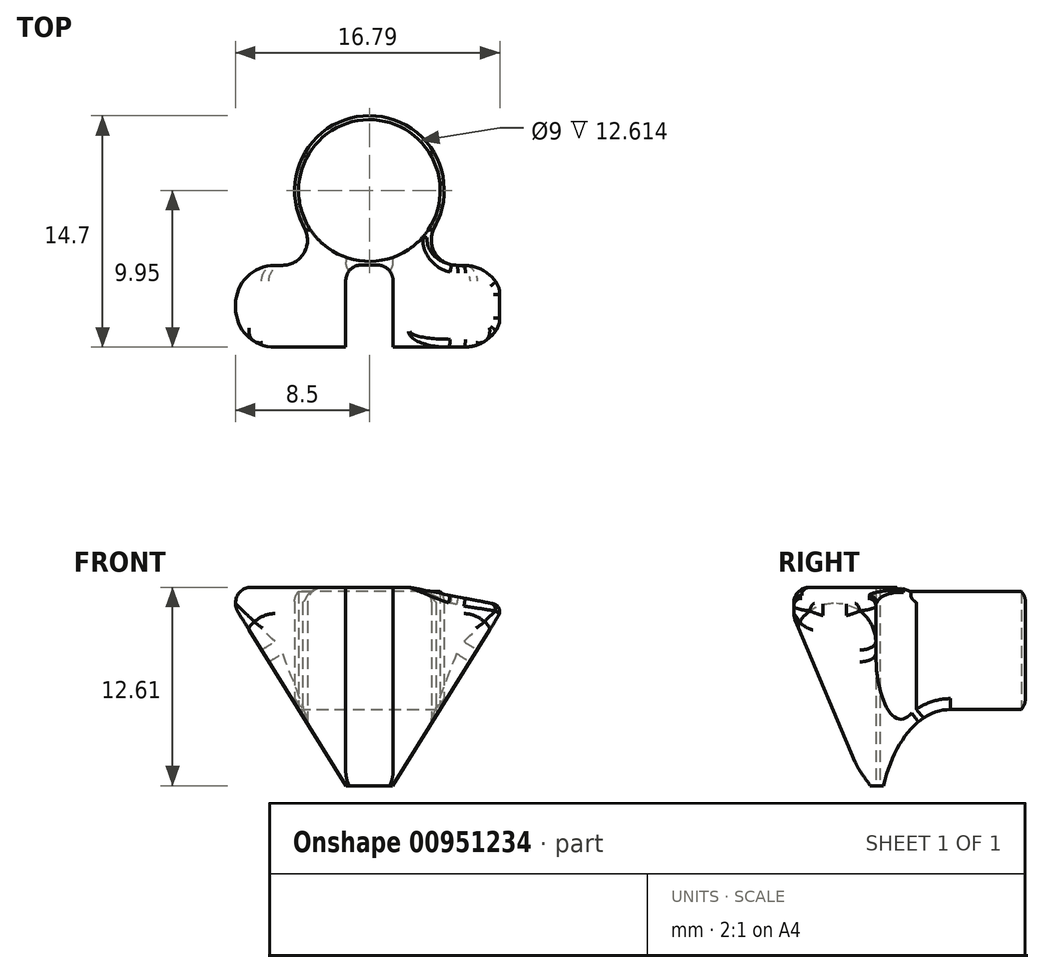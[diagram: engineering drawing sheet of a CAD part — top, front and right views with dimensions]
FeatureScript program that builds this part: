
annotation { "Feature Type Name" : "Feature", "Feature Type Description" : "" }
export const myFeature = defineFeature(function(context is Context, id is Id, definition is map)
    precondition{}
    {
        {
            var Q0;
            Q0=qCreatedBy(makeId("Top.planeOp"),FACE);
            var sketch = newSketch(context, id + "F0", { "sketchPlane" : qUnion([Q0])});
            skCircle(sketch, "E0", {"center": v(0, 0) * mm, "radius": 4.5 * mm});
            skArc(sketch, "E1", {"start": v(4.23, -2.16) * mm, "mid": v(0, 4.75) * mm, "end": v(-4.23, -2.16) * mm});
            skLineSegment(sketch, "E2", {"start": v(5.53, -4.75) * mm, "end": v(6, -4.75) * mm});
            skLineSegment(sketch, "E3", {"start": v(8.5, -7.25) * mm, "end": v(8.5, -7.45) * mm});
            skLineSegment(sketch, "E4", {"start": v(6, -9.95) * mm, "end": v(1.5, -9.95) * mm});
            skLineSegment(sketch, "E5", {"start": v(1.5, -9.95) * mm, "end": v(1.5, -5.73) * mm});
            skPoint(sketch, "E6.end.orphan", {"position": v(0, -5.25) * mm});
            skPoint(sketch, "E7.visualSharp", {"position": v(8.5, -4.75) * mm});
            skArc(sketch, "E7.filletArc", {"start": v(8.5, -7.25) * mm, "mid": v(7.77, -5.48) * mm, "end": v(6, -4.75) * mm});
            skPoint(sketch, "E8.visualSharp", {"position": v(8.5, -9.95) * mm});
            skArc(sketch, "E8.filletArc", {"start": v(6, -9.95) * mm, "mid": v(7.77, -9.22) * mm, "end": v(8.5, -7.45) * mm});
            skLineSegment(sketch, "E9", {"start": v(4.23, -2.16) * mm, "end": v(4.09, -2.46) * mm});
            skPoint(sketch, "E10.newPointA", {"position": v(3, -4.75) * mm});
            skPoint(sketch, "E10.newPointB", {"position": v(0, -4.75) * mm});
            skArc(sketch, "E10.filletArc", {"start": v(4.09, -2.46) * mm, "mid": v(4.18, -4) * mm, "end": v(5.53, -4.75) * mm});
            skLineSegment(sketch, "E11.MirrorCS", {"start": v(-1.5, -9.95) * mm, "end": v(-1.5, -5.73) * mm});
            skArc(sketch, "E12.MirrorCS", {"start": v(-4.09, -2.46) * mm, "mid": v(-4.18, -4) * mm, "end": v(-5.53, -4.75) * mm});
            skLineSegment(sketch, "E13.MirrorCS", {"start": v(-5.53, -4.75) * mm, "end": v(-6, -4.75) * mm});
            skLineSegment(sketch, "E14.MirrorCS", {"start": v(-4.23, -2.16) * mm, "end": v(-4.09, -2.46) * mm});
            skArc(sketch, "E15.MirrorCS", {"start": v(-8.5, -7.25) * mm, "mid": v(-7.77, -5.48) * mm, "end": v(-6, -4.75) * mm});
            skArc(sketch, "E16.MirrorCS", {"start": v(-6, -9.95) * mm, "mid": v(-7.77, -9.22) * mm, "end": v(-8.5, -7.45) * mm});
            skArc(sketch, "E17.trimOffspring", {"start": v(-0.41, -4.73) * mm, "mid": v(0, -4.75) * mm, "end": v(0.41, -4.73) * mm});
            skPoint(sketch, "E18.visualSharp", {"position": v(-1.5, -4.5) * mm});
            skArc(sketch, "E18.filletArc", {"start": v(-0.41, -4.73) * mm, "mid": v(-1.18, -5) * mm, "end": v(-1.5, -5.73) * mm});
            skPoint(sketch, "E19.visualSharp", {"position": v(1.5, -4.5) * mm});
            skArc(sketch, "E19.filletArc", {"start": v(1.5, -5.73) * mm, "mid": v(1.18, -5) * mm, "end": v(0.41, -4.73) * mm});
            skLineSegment(sketch, "E20.trimOffspring", {"start": v(-1.5, -9.95) * mm, "end": v(-6, -9.95) * mm});
            skLineSegment(sketch, "E21.MirrorCS", {"start": v(-8.5, -7.25) * mm, "end": v(-8.5, -7.45) * mm});
            skSolve(sketch);
        }
        {
            var Q0;
            Q0=makeQuery(id+"F0.imprint","IMPRINT",FACE,{"disambiguationData":[TD([[makeQuery(id+"F0.imprint","IMPRINT",EDGE,{"derivedFrom":sQuery(id+"F0.wireOp",EDGE,"E0")}),-1.0]])]});
            extrude(context, id + "F1", {"entities" : qUnion([Q0]), "depth" : 15 * mm, "offsetDistance" : 25 * mm});
        }
        {
            var Q0;
            Q0=qCreatedBy(makeId("Front.planeOp"),FACE);
            var sketch = newSketch(context, id + "F2", { "sketchPlane" : qUnion([Q0])});
            skLineSegment(sketch, "E22", {"start": v(0, 0) * mm, "end": v(-8.66, 13.94) * mm});
            skLineSegment(sketch, "E23", {"start": v(-8.66, 13.94) * mm, "end": v(-8.66, 0) * mm});
            skLineSegment(sketch, "E24", {"start": v(-8.66, 0) * mm, "end": v(0, 0) * mm});
            skLineSegment(sketch, "E25.MirrorCS", {"start": v(0, 0) * mm, "end": v(8.66, 13.94) * mm});
            skLineSegment(sketch, "E26.MirrorCS", {"start": v(8.66, 13.94) * mm, "end": v(8.66, 0) * mm});
            skLineSegment(sketch, "E27.MirrorCS", {"start": v(8.66, 0) * mm, "end": v(0, 0) * mm});
            skSolve(sketch);
        }
        {
            var Q0;
            Q0 = qSketchRegion(id + "F2", true);
            extrude(context, id + "F3", {"entities" : qUnion([Q0]), "operationType" : NewBodyOperationType.REMOVE, "depth" : 25 * mm, "offsetDistance" : 25 * mm});
        }
        {
            var Q0;
            Q0=qCreatedBy(makeId("Right.planeOp"),FACE);
            var sketch = newSketch(context, id + "F4", { "sketchPlane" : qUnion([Q0])});
            skLineSegment(sketch, "E28", {"start": v(-10.13, 13.54) * mm, "end": v(-5.41, 2.39) * mm});
            skLineSegment(sketch, "E29", {"start": v(-4.4, 0) * mm, "end": v(-11.01, 0) * mm});
            skLineSegment(sketch, "E30", {"start": v(-11.01, 0) * mm, "end": v(-11.01, 13.65) * mm});
            skLineSegment(sketch, "E31", {"start": v(-11.01, 13.65) * mm, "end": v(-10.13, 13.54) * mm});
            skLineSegment(sketch, "E32", {"start": v(0, 7.25) * mm, "end": v(5.54, 7.25) * mm});
            skLineSegment(sketch, "E33", {"start": v(5.54, 7.25) * mm, "end": v(5.54, -2.68) * mm});
            skLineSegment(sketch, "E34", {"start": v(5.54, -2.68) * mm, "end": v(0, -2.68) * mm});
            skLineSegment(sketch, "E35", {"start": v(0, -2.68) * mm, "end": v(0, 7.25) * mm});
            skLineSegment(sketch, "E36", {"start": v(-5.41, 2.39) * mm, "end": v(-3.47, 2.39) * mm});
            skLineSegment(sketch, "E37", {"start": v(-3.47, 2.39) * mm, "end": v(-3.47, 0) * mm});
            skLineSegment(sketch, "E38", {"start": v(-3.47, 0) * mm, "end": v(-4.7, 0) * mm});
            skSolve(sketch);
        }
        {
            var Q0;
            Q0 = qSketchRegion(id + "F4", true);
            extrude(context, id + "F5", {"entities" : qUnion([Q0]), "operationType" : NewBodyOperationType.REMOVE, "endBound" : BoundingType.SYMMETRIC, "oppositeDirection" : true, "depth" : 25 * mm, "offsetDistance" : 25 * mm});
        }
        {
            var Q0;
            Q0=makeQuery(id+"F5.boolean.opBoolean","INTERSECT",EDGE,{"disambiguationData":[OD(1.0)],"derivedFrom":[makeQuery(id+"F3.boolean.opBoolean","COPY",FACE,{"derivedFrom":makeQuery(id+"F3.opExtrude","SWEPT_FACE",FACE,{"disambiguationData":[OSD([sQuery(id+"F2.wireOp",EDGE,"E22")])]})}),makeQuery(id+"F5.opExtrude","SWEPT_FACE",FACE,{"disambiguationData":[OSD([sQuery(id+"F4.wireOp",EDGE,"E28")])]})]});
            var Q1;
            Q1=makeQuery(id+"F5.boolean.opBoolean","INTERSECT",EDGE,{"disambiguationData":[OD(1.0)],"derivedFrom":[makeQuery(id+"F3.boolean.opBoolean","COPY",FACE,{"derivedFrom":makeQuery(id+"F3.opExtrude","SWEPT_FACE",FACE,{"disambiguationData":[OSD([sQuery(id+"F2.wireOp",EDGE,"E25.MirrorCS")])]})}),makeQuery(id+"F5.opExtrude","SWEPT_FACE",FACE,{"disambiguationData":[OSD([sQuery(id+"F4.wireOp",EDGE,"E28")])]})]});
            var Q2;
            Q2=makeQuery(id+"F5.boolean.opBoolean","INTERSECT",EDGE,{"derivedFrom":[makeQuery(id+"F1.opExtrude","SWEPT_FACE",FACE,{"disambiguationData":[OSD([sQuery(id+"F0.wireOp",EDGE,"E4")])]}),makeQuery(id+"F5.opExtrude","SWEPT_FACE",FACE,{"disambiguationData":[OSD([sQuery(id+"F4.wireOp",EDGE,"E28")])]})]});
            var Q3;
            Q3=makeQuery(id+"F5.boolean.opBoolean","INTERSECT",EDGE,{"derivedFrom":[makeQuery(id+"F1.opExtrude","SWEPT_FACE",FACE,{"disambiguationData":[OSD([sQuery(id+"F0.wireOp",EDGE,"E20.trimOffspring")])]}),makeQuery(id+"F5.opExtrude","SWEPT_FACE",FACE,{"disambiguationData":[OSD([sQuery(id+"F4.wireOp",EDGE,"E28")])]})]});
            var Q4;
            Q4=makeQuery(id+"F3.boolean.opBoolean","INTERSECT",EDGE,{"derivedFrom":[makeQuery(id+"F1.opExtrude","SWEPT_FACE",FACE,{"disambiguationData":[OSD([sQuery(id+"F0.wireOp",EDGE,"E7.filletArc")])]}),makeQuery(id+"F3.opExtrude","SWEPT_FACE",FACE,{"disambiguationData":[OSD([sQuery(id+"F2.wireOp",EDGE,"E25.MirrorCS")])]})]});
            var Q5;
            Q5=makeQuery(id+"F3.boolean.opBoolean","INTERSECT",EDGE,{"derivedFrom":[makeQuery(id+"F1.opExtrude","SWEPT_FACE",FACE,{"disambiguationData":[OSD([sQuery(id+"F0.wireOp",EDGE,"E15.MirrorCS")])]}),makeQuery(id+"F3.opExtrude","SWEPT_FACE",FACE,{"disambiguationData":[OSD([sQuery(id+"F2.wireOp",EDGE,"E22")])]})]});
            var Q6;
            Q6=makeQuery(id+"F1.opExtrude","CAP_EDGE",EDGE,{"disambiguationData":[OSD([sQuery(id+"F0.wireOp",EDGE,"E4")])],"isStart":false});
            var Q7;
            Q7=makeQuery(id+"F1.opExtrude","CAP_EDGE",EDGE,{"disambiguationData":[OSD([sQuery(id+"F0.wireOp",EDGE,"E20.trimOffspring")])],"isStart":false});
            fillet(context, id + "F6", {"entities" : qUnion([Q0, Q1, Q2, Q3, Q4, Q5, Q6, Q7]), "radius" : 1 * mm, "tangentPropagation" : true, "allowEdgeOverflow" : false});
        }
        {
            var Q0;
            Q0=makeQuery(id+"F5.boolean.opBoolean","INTERSECT",EDGE,{"derivedFrom":[makeQuery(id+"F1.opExtrude","SWEPT_FACE",FACE,{"disambiguationData":[OSD([sQuery(id+"F0.wireOp",EDGE,"E1")])]}),makeQuery(id+"F5.opExtrude","SWEPT_FACE",FACE,{"disambiguationData":[OSD([sQuery(id+"F4.wireOp",EDGE,"E32")])]})]});
            fillet(context, id + "F7", {"entities" : qUnion([Q0]), "radius" : 1 * mm, "tangentPropagation" : true, "allowEdgeOverflow" : false});
        }
        {
            var Q0;
            Q0=makeQuery(id+"F1.opExtrude","CAP_EDGE",EDGE,{"disambiguationData":[OSD([sQuery(id+"F0.wireOp",EDGE,"E1")])],"isStart":false});
            fillet(context, id + "F8", {"entities" : qUnion([Q0]), "radius" : 0.9 * mm, "tangentPropagation" : true, "allowEdgeOverflow" : false});
        }
        {
            var Q0;
            Q0=qCreatedBy(makeId("Front.planeOp"),FACE);
            var sketch = newSketch(context, id + "F9", { "sketchPlane" : qUnion([Q0])});
            skLineSegment(sketch, "E39", {"start": v(0, 15.5) * mm, "end": v(-10.88, 13.36) * mm});
            skLineSegment(sketch, "E40", {"start": v(-10.88, 13.36) * mm, "end": v(-10.88, 15.98) * mm});
            skLineSegment(sketch, "E41", {"start": v(0, 15.5) * mm, "end": v(-10.88, 15.98) * mm});
            skLineSegment(sketch, "E42.MirrorCS", {"start": v(0, 15.5) * mm, "end": v(10.88, 15.98) * mm});
            skLineSegment(sketch, "E43.MirrorCS", {"start": v(10.88, 13.36) * mm, "end": v(10.88, 15.98) * mm});
            skLineSegment(sketch, "E44.MirrorCS", {"start": v(0, 15.5) * mm, "end": v(10.88, 13.36) * mm});
            skSolve(sketch);
        }
        {
            var Q0;
            Q0=makeQuery(id+"F9.imprint","IMPRINT",FACE,{"disambiguationData":[TD([[makeQuery(id+"F9.imprint","IMPRINT",EDGE,{"derivedFrom":sQuery(id+"F9.wireOp",EDGE,"E42.MirrorCS")}),-1.0]])]});
            extrude(context, id + "F10", {"entities" : qUnion([Q0]), "operationType" : NewBodyOperationType.REMOVE, "depth" : 25 * mm, "offsetDistance" : 25 * mm, "hasSecondDirection" : true, "secondDirectionOppositeDirection" : false, "secondDirectionDepth" : 3 * mm});
        }
        {
            var Q0;
            Q0=makeQuery(id+"F10.boolean.opBoolean","INTERSECT",EDGE,{"derivedFrom":[makeQuery(id+"F6.opFillet","BLEND_FACE",FACE,{"disambiguationData":[OSD([sQuery(id+"F0.wireOp",EDGE,"E4")])]}),makeQuery(id+"F10.opExtrude","SWEPT_FACE",FACE,{"disambiguationData":[OSD([sQuery(id+"F9.wireOp",EDGE,"E44.MirrorCS")])]})]});
            fillet(context, id + "F11", {"entities" : qUnion([Q0]), "radius" : 0.5 * mm, "tangentPropagation" : true, "allowEdgeOverflow" : false});
        }
    });
